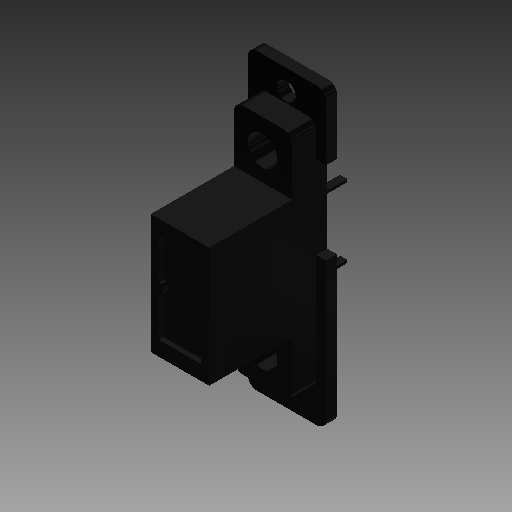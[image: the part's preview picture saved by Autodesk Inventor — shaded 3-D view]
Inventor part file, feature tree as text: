
AUTODESK INVENTOR PART (.ipt)
format: ipt  version: 2018 (Build 220112000, 112)  size: 212,480 bytes
history: native  units: in
note: dims shown in document units (in); Inventor stores cm internally (conversion verified against a paired STEP export)
features: sketch x8, extrude x6, reference x3, fillet x2, hole x2, plane x1, pattern_linear x1
ambient origin geometry x8: Origin, YZ Plane, XZ Plane, XY Plane, X Axis, Y Axis, Z Axis, Center Point
bodies: Body1 (feature_tree)
feature tree (23):
  plane  "Work Plane4"
  extrude  "Extrusion3"  Depth=0.25in
  extrude  "Extrusion4"  Depth=0.998in
  fillet  "Fillet2"  Radius=0.102in
  extrude  "Extrusion5"  Depth=1.26in
  fillet  "Fillet3"  Radius=0.335in
  hole  "Hole2"  [1 undecoded]
  hole  "Hole3"  [1 undecoded]
  extrude  "Extrusion6"  Depth=0.031in
  pattern_linear  "Rectangular Pattern1"  Spacing1=0.102in  [1 undecoded]
  extrude  "Extrusion7"  Depth=0.146in TaperAngle=0.0deg
  extrude  "Extrusion8"  Depth=0.3in
  sketch  "Sketch4"  dims[d15=0.512in d16=0.25in]
  reference  "Reference4"
  sketch  "Sketch5"  dims[d17=0.356in d18=0.0in d19=0.998in d21=0.102in d22=0.0in]
  sketch  "Sketch6"  dims[d23=0.039in d24=1.26in d25=0.335in]
  sketch  "Sketch7"  dims[d26=0.047in d27=0.0in d28=0.039in]
  reference  "Reference5"
  reference  "Reference6"
  sketch  "Sketch8"  dims[d29=0.126in d30=0.75in d31=0.375in d32=0.25in d33=0.5635in d34=1.0in d35=0.8108in d36=1.087in]
  sketch  "Sketch9"  dims[d37=0.079in d38=0.75in d39=0.375in d40=0.25in d41=0.5635in d42=1.0in d43=0.8108in d44=0.031in]
  sketch  "Sketch10"  dims[d45=0.012in]
  sketch  "Sketch11"  dims[d46=0.474in d47=0.102in d48=0.146in d49=0.0in d50=0.7874in d52=0.3in d53=0.7874in d55=0.1in d56=0.276in d57=0.354in d58=0.043in d59=0.146in d60=0.0in d61=0.02in d62=0.0in]
note: 3 required parameter values undecoded (feature->parameter linkage not recoverable at this tier; creation-order binding heuristic only, values carry confidence <= 0.55)
